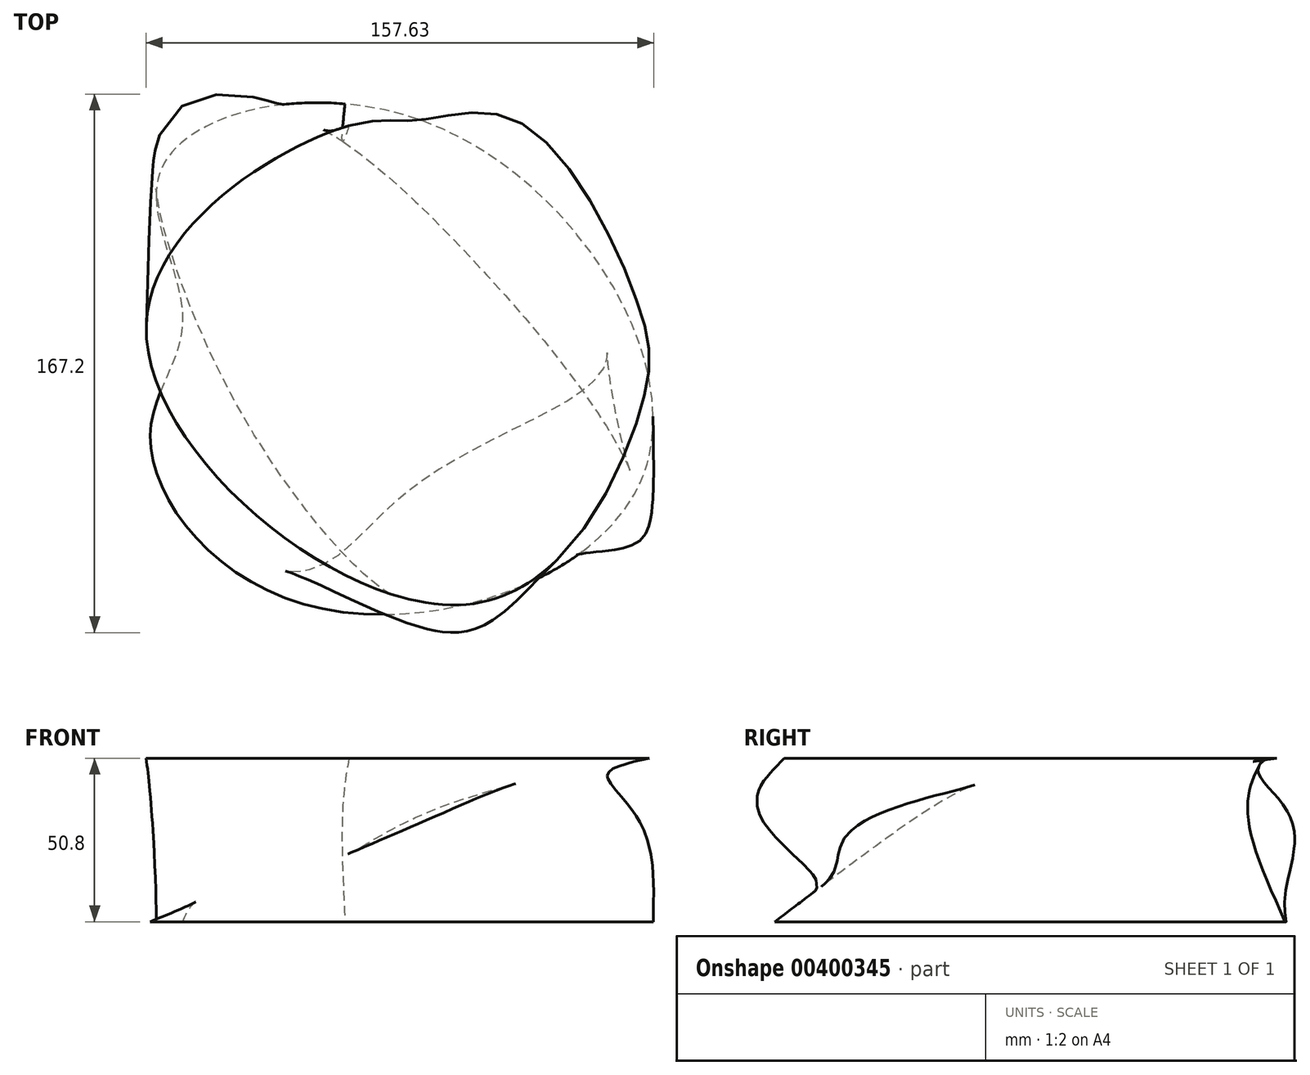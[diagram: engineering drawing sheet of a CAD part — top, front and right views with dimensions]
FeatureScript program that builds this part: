
annotation { "Feature Type Name" : "Feature", "Feature Type Description" : "" }
export const myFeature = defineFeature(function(context is Context, id is Id, definition is map)
    precondition{}
    {
        {
            var Q0;
            Q0=qCreatedBy(makeId("Top.planeOp"),FACE);
            cPlane(context, id + "F0", {"entities" : qUnion([Q0]), "cplaneType" : CPlaneType.OFFSET, "offset" : 25.4 * mm, "width" : 152.4 * mm, "height" : 152.4 * mm});
        }
        {
            var Q0;
            Q0=qCreatedBy(id+"F0.planeOp",FACE);
            cPlane(context, id + "F1", {"entities" : qUnion([Q0]), "cplaneType" : CPlaneType.OFFSET, "offset" : 25.4 * mm, "width" : 152.4 * mm, "height" : 152.4 * mm});
        }
        {
            var Q0;
            Q0=qCreatedBy(id+"F1.planeOp",FACE);
            var sketch = newSketch(context, id + "F2", { "sketchPlane" : qUnion([Q0])});
            skFitSpline(sketch, "E0", {"points": [v(-14.75, 73.18) * mm, v(-77.75, 10.72) * mm, v(22.07, -75.46) * mm, v(75.64, -15.63) * mm, v(75, 17.84) * mm, v(37.68, 74.55) * mm, v(6.48, 74.86) * mm, v(-14.75, 73.18) * mm]});
            skSolve(sketch);
        }
        {
            var Q0;
            Q0=qCreatedBy(id+"F0.planeOp",FACE);
            var sketch = newSketch(context, id + "F3", { "sketchPlane" : qUnion([Q0])});
            skFitSpline(sketch, "E1", {"points": [v(-25.26, 74.73) * mm, v(-75.48, 59.4) * mm, v(-5.45, -77.42) * mm, v(-4.25, -47.19) * mm, v(75.01, -55.44) * mm, v(-25.26, 74.73) * mm]});
            skSolve(sketch);
        }
        {
            var Q0;
            Q0=qCreatedBy(makeId("Top.planeOp"),FACE);
            var sketch = newSketch(context, id + "F4", { "sketchPlane" : qUnion([Q0])});
            skFitSpline(sketch, "E2", {"points": [v(-27.16, -75.87) * mm, v(77.02, -34.4) * mm, v(12.3, 73.06) * mm, v(-73.06, 59.77) * mm, v(-66.43, 13.16) * mm, v(-76.52, -23.67) * mm, v(-27.16, -75.87) * mm]});
            skSolve(sketch);
        }
        {
            var Q0;
            Q0=makeQuery(id+"F2.imprint","IMPRINT",FACE,{"disambiguationData":[TD([[makeQuery(id+"F2.imprint","IMPRINT",EDGE,{"derivedFrom":sQuery(id+"F2.wireOp",EDGE,"E0")}),1.0]])]});
            var Q1;
            Q1=makeQuery(id+"F3.imprint","IMPRINT",FACE,{"disambiguationData":[TD([[makeQuery(id+"F3.imprint","IMPRINT",EDGE,{"derivedFrom":sQuery(id+"F3.wireOp",EDGE,"E1")}),1.0]])]});
            var Q2;
            Q2=makeQuery(id+"F4.imprint","IMPRINT",FACE,{"disambiguationData":[TD([[makeQuery(id+"F4.imprint","IMPRINT",EDGE,{"derivedFrom":sQuery(id+"F4.wireOp",EDGE,"E2")}),1.0]])]});
            loft(context, id + "F5", {"sheetProfilesArray" : [{ "sheetProfileEntities" : qUnion([Q0]) }, { "sheetProfileEntities" : qUnion([Q1]) }, { "sheetProfileEntities" : qUnion([Q2]) }]});
        }
    });
